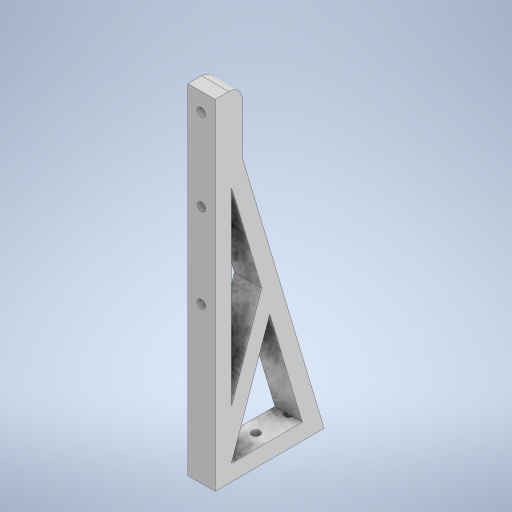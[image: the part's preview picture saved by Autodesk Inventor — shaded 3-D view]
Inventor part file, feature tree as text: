
AUTODESK INVENTOR PART (.ipt)
format: ipt  version: 2023 (Build 270158000, 158)  size: 383,488 bytes
history: native  units: mm
features: extrude x9, sketch x9, other x2, fillet x1, projected_geometry x1
ambient origin geometry x8: Origin, YZ Plane, XZ Plane, XY Plane, X Axis, Y Axis, Z Axis, Center Point
bodies: Body1 (feature_tree)
feature tree (22):
  other  "솔리드1"
  extrude  "돌출1"  Depth=66.0mm
  extrude  "돌출2"  Depth=10.0mm
  other  "작업 평면1"
  extrude  "돌출3"  Depth=10.0mm
  extrude  "돌출4"  Depth=30.0mm
  extrude  "돌출5"  Depth=50.0mm TaperAngle=0.0deg
  extrude  "돌출6"  Depth=28.0mm
  extrude  "돌출7"  Depth=150.0mm
  extrude  "돌출8"  Depth=10.0mm TaperAngle=0.0deg
  extrude  "돌출9"  Depth=16.0mm
  fillet  "모깎기3"  Radius=6.0mm
  sketch  "스케치1"
  sketch  "스케치2"
  sketch  "스케치3"
  sketch  "스케치4"
  sketch  "스케치5"
  sketch  "스케치6"
  sketch  "스케치7"
  sketch  "스케치8"
  sketch  "스케치9"
  projected_geometry  "투영된 루프1"
